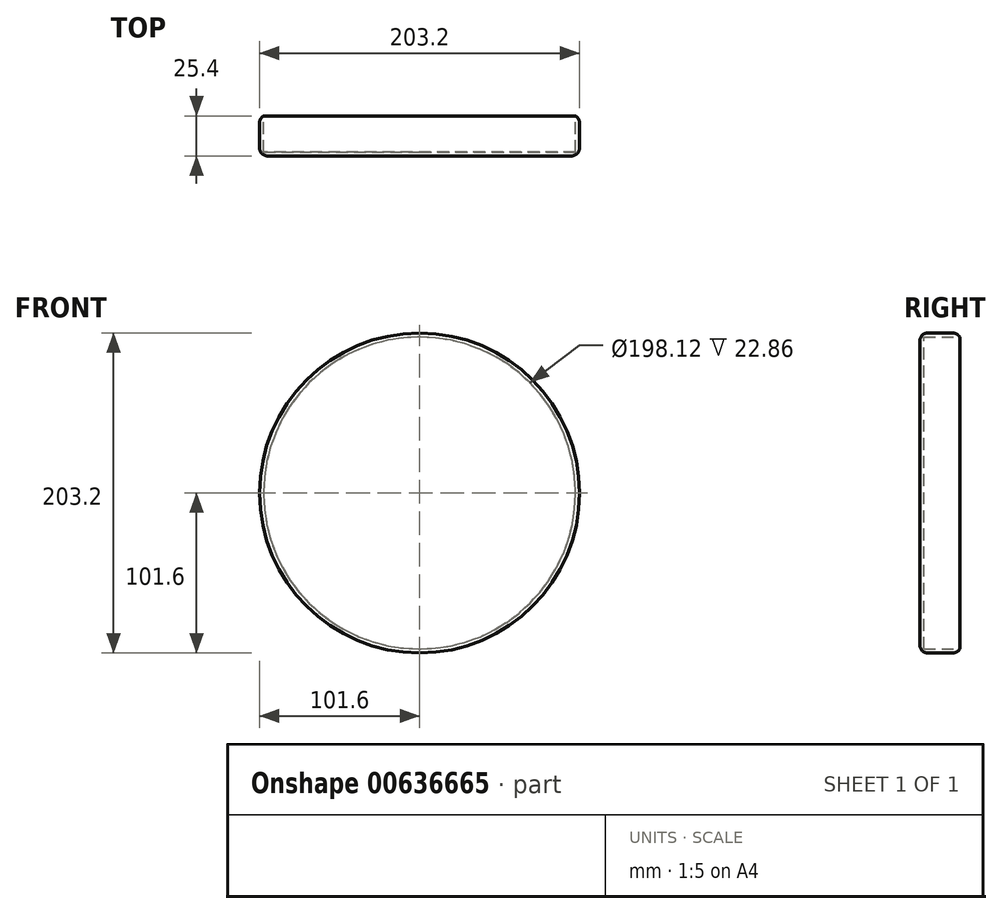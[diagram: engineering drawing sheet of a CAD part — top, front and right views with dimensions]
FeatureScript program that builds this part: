
annotation { "Feature Type Name" : "Feature", "Feature Type Description" : "" }
export const myFeature = defineFeature(function(context is Context, id is Id, definition is map)
    precondition{}
    {
        {
            var Q0;
            Q0=qCreatedBy(makeId("Front.planeOp"),FACE);
            var sketch = newSketch(context, id + "F0", { "sketchPlane" : qUnion([Q0])});
            skCircle(sketch, "E0", {"center": v(0, 0) * mm, "radius": 101.6 * mm});
            skSolve(sketch);
        }
        {
            var Q0;
            Q0 = qSketchRegion(id + "F0", true);
            extrude(context, id + "F1", {"entities" : qUnion([Q0]), "depth" : 25.4 * mm, "offsetDistance" : 25.4 * mm});
        }
        {
            var Q0;
            Q0=makeQuery(id+"F1.opExtrude","CAP_FACE",FACE,{"disambiguationData":[OSD([sQuery(id+"F0.wireOp",EDGE,"E0")])],"isStart":true});
            shell(context, id + "F2", {"entities" : qUnion([Q0]), "thickness" : 2.54 * mm});
        }
        {
            var Q0;
            Q0=makeQuery(id+"F1.opExtrude","CAP_FACE",FACE,{"disambiguationData":[OSD([sQuery(id+"F0.wireOp",EDGE,"E0")])],"isStart":false});
            var Q1;
            Q1=makeQuery(id+"F1.opExtrude","CAP_EDGE",EDGE,{"disambiguationData":[OSD([sQuery(id+"F0.wireOp",EDGE,"E0")])],"isStart":true});
            fillet(context, id + "F3", {"entities" : qUnion([Q0, Q1]), "radius" : 5.08 * mm, "tangentPropagation" : true, "allowEdgeOverflow" : false});
        }
    });
